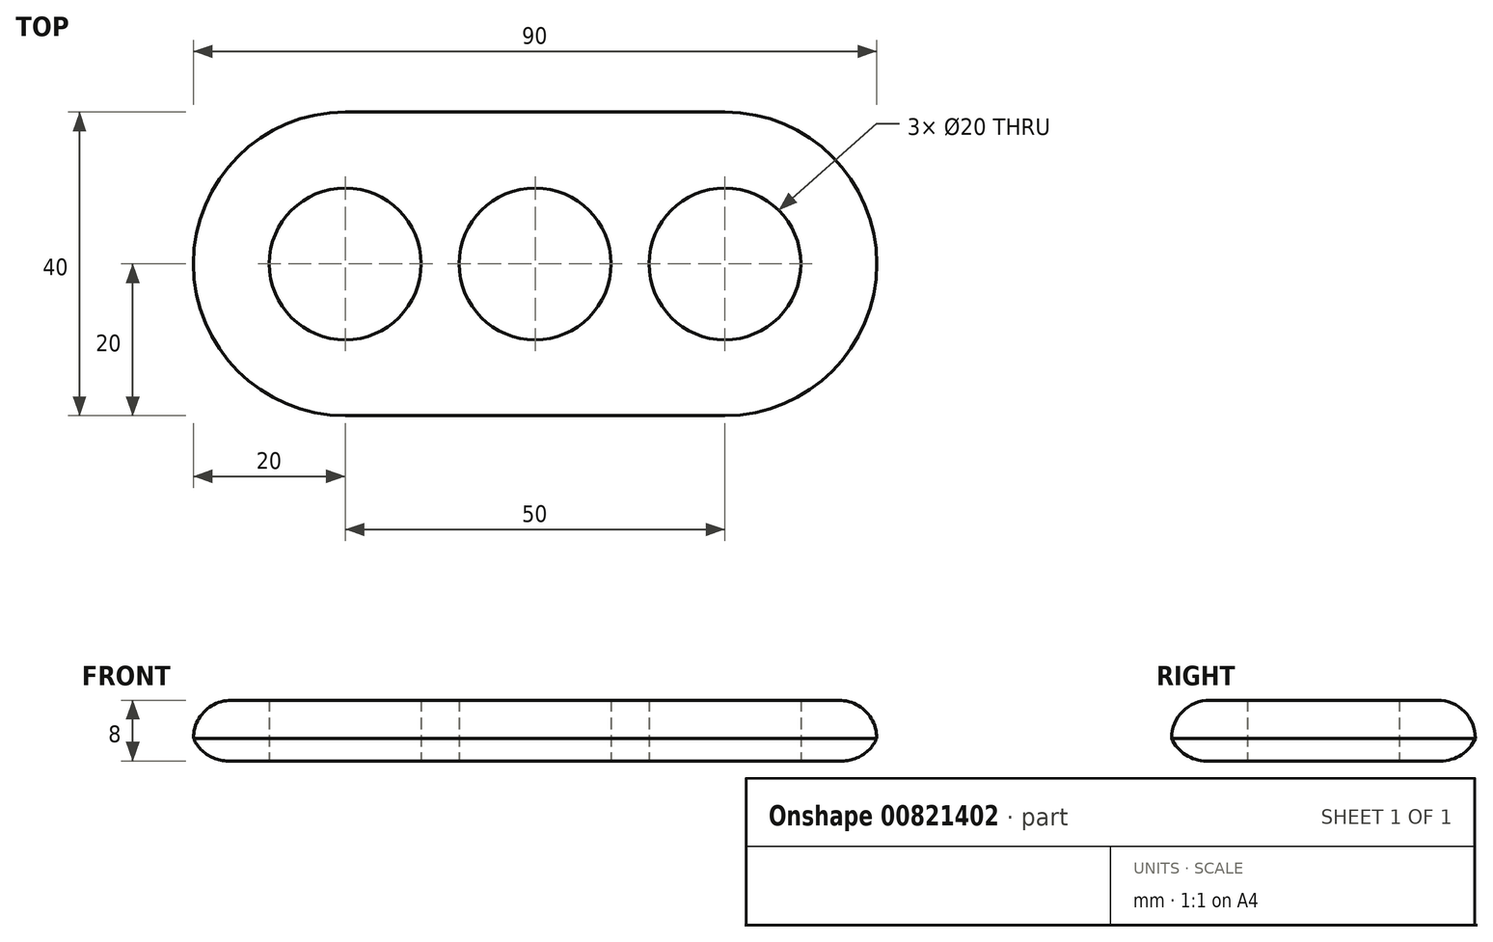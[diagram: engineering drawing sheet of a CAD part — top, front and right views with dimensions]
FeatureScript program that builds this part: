
annotation { "Feature Type Name" : "Feature", "Feature Type Description" : "" }
export const myFeature = defineFeature(function(context is Context, id is Id, definition is map)
    precondition{}
    {
        {
            var Q0;
            Q0=qCreatedBy(makeId("Top.planeOp"),FACE);
            var sketch = newSketch(context, id + "F0", { "sketchPlane" : qUnion([Q0])});
            skCircle(sketch, "E0", {"center": v(0, 0) * mm, "radius": 10 * mm});
            skCircle(sketch, "E1", {"center": v(-25, 0) * mm, "radius": 10 * mm});
            skCircle(sketch, "E2.MirrorC", {"center": v(25, 0) * mm, "radius": 10 * mm});
            skArc(sketch, "E3", {"start": v(-25, 20) * mm, "mid": v(-45, 0) * mm, "end": v(-25, -20) * mm});
            skArc(sketch, "E4.MirrorC", {"start": v(25, 20) * mm, "mid": v(45, 0) * mm, "end": v(25, -20) * mm});
            skLineSegment(sketch, "E5", {"start": v(-25, 20) * mm, "end": v(25, 20) * mm});
            skLineSegment(sketch, "E6.MirrorCS", {"start": v(-25, -20) * mm, "end": v(25, -20) * mm});
            skSolve(sketch);
        }
        {
            var Q0;
            Q0=makeQuery(id+"F0.imprint","IMPRINT",FACE,{"disambiguationData":[TD([[makeQuery(id+"F0.imprint","IMPRINT",EDGE,{"derivedFrom":sQuery(id+"F0.wireOp",EDGE,"E0")}),-1.0]])]});
            extrude(context, id + "F1", {"entities" : qUnion([Q0]), "endBound" : BoundingType.SYMMETRIC, "depth" : 8 * mm, "offsetDistance" : 25 * mm});
        }
        {
            var Q0;
            Q0=makeQuery(id+"F1.opExtrude","CAP_EDGE",EDGE,{"disambiguationData":[OSD([sQuery(id+"F0.wireOp",EDGE,"E5")])],"isStart":false});
            var Q1;
            Q1=makeQuery(id+"F1.opExtrude","CAP_EDGE",EDGE,{"disambiguationData":[OSD([sQuery(id+"F0.wireOp",EDGE,"E3")])],"isStart":false});
            var Q2;
            Q2=makeQuery(id+"F1.opExtrude","CAP_EDGE",EDGE,{"disambiguationData":[OSD([sQuery(id+"F0.wireOp",EDGE,"E6.MirrorCS")])],"isStart":false});
            var Q3;
            Q3=makeQuery(id+"F1.opExtrude","CAP_EDGE",EDGE,{"disambiguationData":[OSD([sQuery(id+"F0.wireOp",EDGE,"E4.MirrorC")])],"isStart":false});
            fillet(context, id + "F2", {"entities" : qUnion([Q0, Q1, Q2, Q3]), "radius" : 5 * mm, "tangentPropagation" : true, "allowEdgeOverflow" : false});
        }
        {
            var Q0;
            Q0=makeQuery(id+"F1.opExtrude","CAP_EDGE",EDGE,{"disambiguationData":[OSD([sQuery(id+"F0.wireOp",EDGE,"E4.MirrorC")])],"isStart":true});
            var Q1;
            {var subQ0=sQuery(id+"F0.wireOp",EDGE,"E5");Q1=makeQuery(id+"F2.opFillet","BLEND_EDGE",EDGE,{"blendedFrom":[makeQuery(id+"F1.opExtrude","CAP_EDGE",EDGE,{"disambiguationData":[OSD([subQ0])],"isStart":false}),makeQuery(id+"F1.opExtrude","SWEPT_FACE",FACE,{"disambiguationData":[OSD([subQ0])]})],"blendedInto":[makeQuery(id+"F1.opExtrude","SWEPT_FACE",FACE,{"disambiguationData":[OSD([subQ0])]})]});}
            var Q2;
            Q2=makeQuery(id+"F1.opExtrude","CAP_EDGE",EDGE,{"disambiguationData":[OSD([sQuery(id+"F0.wireOp",EDGE,"E3")])],"isStart":true});
            var Q3;
            Q3=makeQuery(id+"F1.opExtrude","CAP_EDGE",EDGE,{"disambiguationData":[OSD([sQuery(id+"F0.wireOp",EDGE,"E6.MirrorCS")])],"isStart":true});
            fillet(context, id + "F3", {"entities" : qUnion([Q0, Q1, Q2, Q3]), "radius" : 5 * mm, "tangentPropagation" : true, "allowEdgeOverflow" : false});
        }
    });
